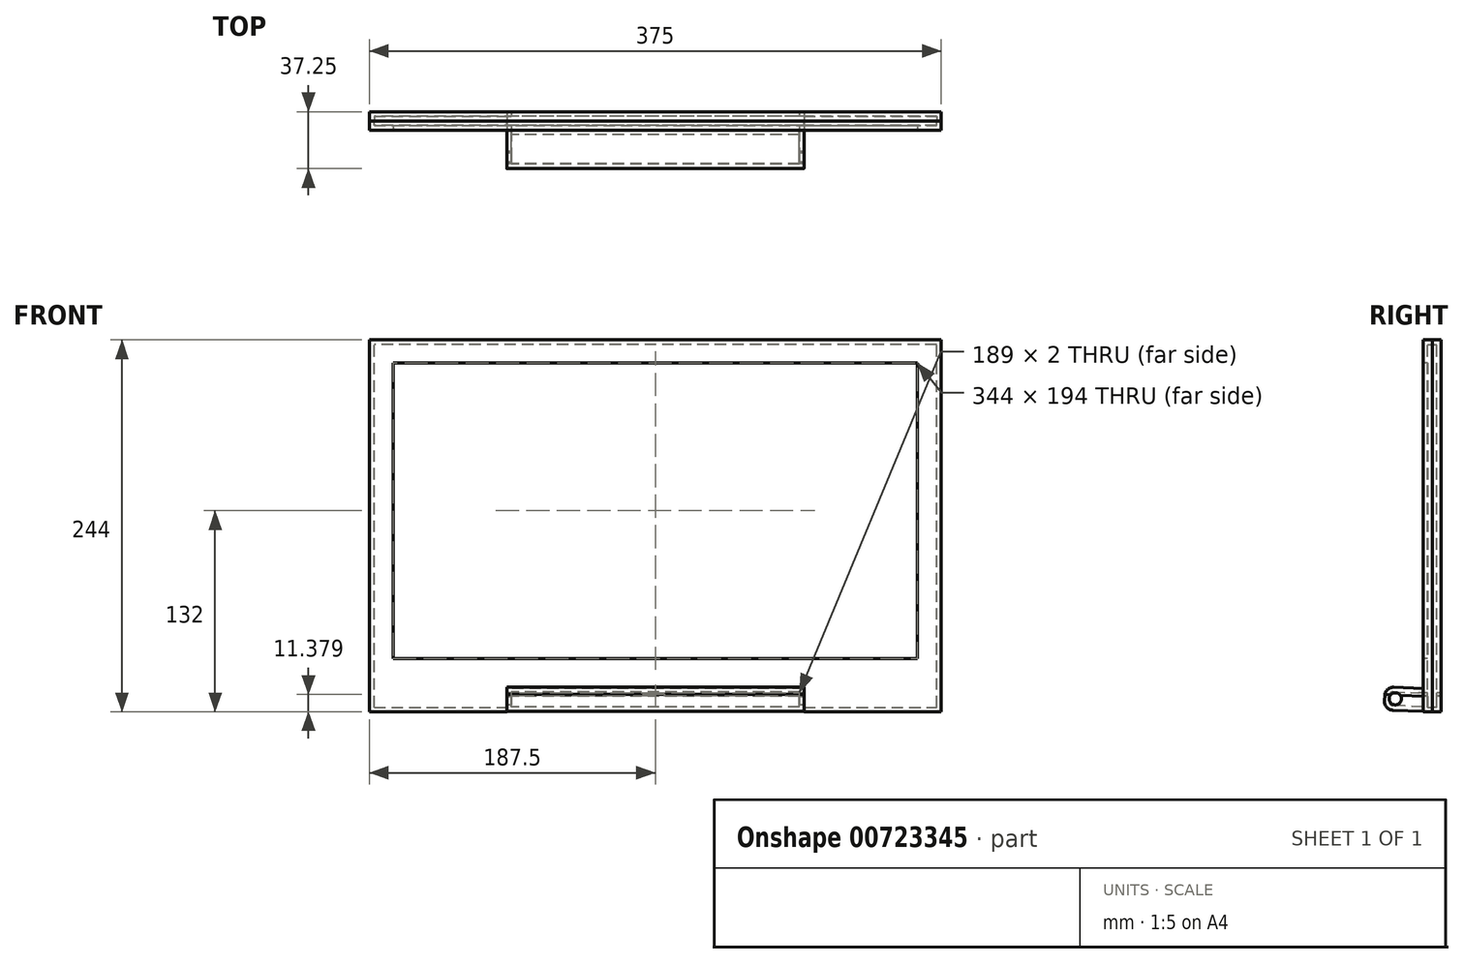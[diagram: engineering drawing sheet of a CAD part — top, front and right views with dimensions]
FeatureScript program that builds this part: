
annotation { "Feature Type Name" : "Feature", "Feature Type Description" : "" }
export const myFeature = defineFeature(function(context is Context, id is Id, definition is map)
    precondition{}
    {
        {
            var Q0;
            Q0=qCreatedBy(makeId("Front.planeOp"),FACE);
            var sketch = newSketch(context, id + "F0", { "sketchPlane" : qUnion([Q0])});
            skLineSegment(sketch, "E0.bottom", {"start": v(187.5, -117) * mm, "end": v(-187.5, -117) * mm});
            skLineSegment(sketch, "E0.top", {"start": v(187.5, 117) * mm, "end": v(-187.5, 117) * mm});
            skLineSegment(sketch, "E0.left", {"start": v(187.5, -117) * mm, "end": v(187.5, 117) * mm});
            skLineSegment(sketch, "E0.right", {"start": v(-187.5, -117) * mm, "end": v(-187.5, 117) * mm});
            skPoint(sketch, "E0.middle", {"position": v(0, 0) * mm});
            skSolve(sketch);
        }
        {
            var Q0;
            Q0=makeQuery(id+"F0.imprint","IMPRINT",FACE,{"disambiguationData":[TD([[makeQuery(id+"F0.imprint","IMPRINT",EDGE,{"derivedFrom":sQuery(id+"F0.wireOp",EDGE,"E0.bottom")}),-1.0]])]});
            extrude(context, id + "F1", {"entities" : qUnion([Q0]), "depth" : 6 * mm, "offsetDistance" : 25 * mm});
        }
        {
            var Q0;
            Q0=makeQuery(id+"F1.opExtrude","CAP_FACE",FACE,{"disambiguationData":[OSD([sQuery(id+"F0.wireOp",EDGE,"E0.bottom"),sQuery(id+"F0.wireOp",EDGE,"E0.top"),sQuery(id+"F0.wireOp",EDGE,"E0.left"),sQuery(id+"F0.wireOp",EDGE,"E0.right")])],"isStart":false});
            var sketch = newSketch(context, id + "F2", { "sketchPlane" : qUnion([Q0])});
            skLineSegment(sketch, "E1.bottom", {"start": v(-187.5, -117) * mm, "end": v(187.5, -117) * mm});
            skLineSegment(sketch, "E1.top", {"start": v(-187.5, -127) * mm, "end": v(187.5, -127) * mm});
            skLineSegment(sketch, "E1.left", {"start": v(-187.5, -117) * mm, "end": v(-187.5, -127) * mm});
            skLineSegment(sketch, "E1.right", {"start": v(187.5, -117) * mm, "end": v(187.5, -127) * mm});
            skSolve(sketch);
        }
        {
            var Q0;
            Q0=qSketchRegion(id+"F2",true);
            extrude(context, id + "F3", {"entities" : qUnion([Q0]), "operationType" : NewBodyOperationType.ADD, "oppositeDirection" : true, "depth" : 6 * mm, "offsetDistance" : 25 * mm});
        }
        {
            var Q0;
            Q0=makeQuery(id+"F3.boolean.opBoolean","MERGE",FACE,{"derivedFrom":[makeQuery(id+"F1.opExtrude","CAP_FACE",FACE,{"disambiguationData":[OSD([sQuery(id+"F0.wireOp",EDGE,"E0.bottom"),sQuery(id+"F0.wireOp",EDGE,"E0.top"),sQuery(id+"F0.wireOp",EDGE,"E0.left"),sQuery(id+"F0.wireOp",EDGE,"E0.right")])],"isStart":false}),makeQuery(id+"F3.opExtrude","CAP_FACE",FACE,{"disambiguationData":[OSD([sQuery(id+"F2.wireOp",EDGE,"E1.bottom"),sQuery(id+"F2.wireOp",EDGE,"E1.top"),sQuery(id+"F2.wireOp",EDGE,"E1.left"),sQuery(id+"F2.wireOp",EDGE,"E1.right")])],"isStart":true})]});
            shell(context, id + "F4", {"entities" : qUnion([Q0]), "thickness" : 3 * mm});
        }
        {
            var Q0;
            Q0=makeQuery(id+"F3.boolean.opBoolean","MERGE",FACE,{"derivedFrom":[makeQuery(id+"F1.opExtrude","CAP_FACE",FACE,{"disambiguationData":[OSD([sQuery(id+"F0.wireOp",EDGE,"E0.bottom"),sQuery(id+"F0.wireOp",EDGE,"E0.top"),sQuery(id+"F0.wireOp",EDGE,"E0.left"),sQuery(id+"F0.wireOp",EDGE,"E0.right")])],"isStart":false}),makeQuery(id+"F3.opExtrude","CAP_FACE",FACE,{"disambiguationData":[OSD([sQuery(id+"F2.wireOp",EDGE,"E1.bottom"),sQuery(id+"F2.wireOp",EDGE,"E1.top"),sQuery(id+"F2.wireOp",EDGE,"E1.left"),sQuery(id+"F2.wireOp",EDGE,"E1.right")])],"isStart":true})]});
            var sketch = newSketch(context, id + "F5", { "sketchPlane" : qUnion([Q0])});
            skLineSegment(sketch, "E2.bottom", {"start": v(-187.5, 117) * mm, "end": v(187.5, 117) * mm});
            skLineSegment(sketch, "E2.top", {"start": v(-187.5, -127) * mm, "end": v(187.5, -127) * mm});
            skLineSegment(sketch, "E2.left", {"start": v(-187.5, 117) * mm, "end": v(-187.5, -127) * mm});
            skLineSegment(sketch, "E2.right", {"start": v(187.5, 117) * mm, "end": v(187.5, -127) * mm});
            skSolve(sketch);
        }
        {
            var Q0;
            Q0=qSketchRegion(id+"F5",true);
            extrude(context, id + "F6", {"entities" : qUnion([Q0]), "depth" : 6 * mm, "offsetDistance" : 25 * mm});
        }
        {
            var Q0;
            Q0=makeQuery(id+"F6.opExtrude","CAP_FACE",FACE,{"disambiguationData":[OSD([sQuery(id+"F5.wireOp",EDGE,"E2.bottom"),sQuery(id+"F5.wireOp",EDGE,"E2.top"),sQuery(id+"F5.wireOp",EDGE,"E2.left"),sQuery(id+"F5.wireOp",EDGE,"E2.right")])],"isStart":true});
            shell(context, id + "F7", {"entities" : qUnion([Q0]), "thickness" : 3 * mm});
        }
        {
            var Q0;
            Q0=makeQuery(id+"F6.opExtrude","CAP_FACE",FACE,{"disambiguationData":[OSD([sQuery(id+"F5.wireOp",EDGE,"E2.bottom"),sQuery(id+"F5.wireOp",EDGE,"E2.top"),sQuery(id+"F5.wireOp",EDGE,"E2.left"),sQuery(id+"F5.wireOp",EDGE,"E2.right")])],"isStart":false});
            var sketch = newSketch(context, id + "F8", { "sketchPlane" : qUnion([Q0])});
            skPoint(sketch, "E3", {"position": v(0, 0) * mm});
            skPoint(sketch, "E4", {"position": v(0, 5) * mm});
            skLineSegment(sketch, "E5.bottom", {"start": v(-172, 102) * mm, "end": v(172, 102) * mm});
            skLineSegment(sketch, "E5.top", {"start": v(-172, -92) * mm, "end": v(172, -92) * mm});
            skLineSegment(sketch, "E5.left", {"start": v(-172, 102) * mm, "end": v(-172, -92) * mm});
            skLineSegment(sketch, "E5.right", {"start": v(172, 102) * mm, "end": v(172, -92) * mm});
            skSolve(sketch);
        }
        {
            var Q0;
            Q0=qSketchRegion(id+"F8",true);
            extrude(context, id + "F9", {"entities" : qUnion([Q0]), "operationType" : NewBodyOperationType.REMOVE, "oppositeDirection" : true, "depth" : 3 * mm, "offsetDistance" : 25 * mm});
        }
        {
            var Q0;
            Q0=makeQuery(id+"F6.opExtrude","SWEPT_FACE",FACE,{"disambiguationData":[OSD([sQuery(id+"F5.wireOp",EDGE,"E2.left")])]});
            var sketch = newSketch(context, id + "F10", { "sketchPlane" : qUnion([Q0])});
            skLineSegment(sketch, "E6", {"start": v(6, -127) * mm, "end": v(37.47, -125.7) * mm});
            skLineSegment(sketch, "E7", {"start": v(37.47, -125.7) * mm, "end": v(36.86, -110.72) * mm});
            skLineSegment(sketch, "E8", {"start": v(36.86, -110.72) * mm, "end": v(12, -111.74) * mm});
            skPoint(sketch, "E9", {"position": v(37.06, -115.72) * mm});
            skLineSegment(sketch, "E10", {"start": v(37.06, -115.72) * mm, "end": v(12, -116.75) * mm});
            skLineSegment(sketch, "E11", {"start": v(12, -111.74) * mm, "end": v(12, -116.75) * mm});
            skLineSegment(sketch, "E12", {"start": v(12, -116.75) * mm, "end": v(6, -117) * mm});
            skLineSegment(sketch, "E13", {"start": v(6, -117) * mm, "end": v(6, -127) * mm});
            skSolve(sketch);
        }
        {
            var Q0;
            {var subQ0=sQuery(id+"F10.wireOp",EDGE,"E8");Q0=makeQuery(id+"F10.imprint","IMPRINT",FACE,{"disambiguationData":[TD([[makeQuery(id+"F10.imprint","IMPRINT",EDGE,{"derivedFrom":subQ0}),1.0]])]});}
            extrude(context, id + "F11", {"entities" : qUnion([Q0]), "oppositeDirection" : true, "depth" : 195 * mm, "offsetDistance" : 25 * mm});
        }
        {
            var Q0;
            {var subQ5=sQuery(id+"F10.wireOp",EDGE,"E10");Q0=makeQuery(id+"F10.imprint","IMPRINT",FACE,{"disambiguationData":[TD([[makeQuery(id+"F10.imprint","IMPRINT",EDGE,{"derivedFrom":subQ5}),1.0]])]});}
            var Q1;
            {var subQ5=sQuery(id+"F10.wireOp",EDGE,"E12");Q1=makeQuery(id+"F10.imprint","IMPRINT",FACE,{"disambiguationData":[TD([[makeQuery(id+"F10.imprint","IMPRINT",EDGE,{"derivedFrom":subQ5}),1.0]])]});}
            extrude(context, id + "F12", {"entities" : qUnion([Q0, Q1]), "oppositeDirection" : true, "depth" : 195 * mm, "offsetDistance" : 25 * mm});
        }
        {
            var Q0;
            Q0=makeQuery(id+"F11.opExtrude","SWEPT_BODY",BODY,{"disambiguationData":[OSD([sQuery(id+"F10.wireOp",EDGE,"E7"),sQuery(id+"F10.wireOp",EDGE,"E8"),sQuery(id+"F10.wireOp",EDGE,"E10"),sQuery(id+"F10.wireOp",EDGE,"E11")])]});
            var Q1;
            Q1=makeQuery(id+"F12.opExtrude","SWEPT_BODY",BODY,{"disambiguationData":[OSD([sQuery(id+"F10.wireOp",EDGE,"E6"),sQuery(id+"F10.wireOp",EDGE,"E7"),sQuery(id+"F10.wireOp",EDGE,"E10"),sQuery(id+"F10.wireOp",EDGE,"E12"),sQuery(id+"F10.wireOp",EDGE,"E13")])]});
            transform(context, id + "F13", {"entities" : qUnion([Q0, Q1]), "transformType" : TransformType.TRANSLATION_3D, "dx" : 90 * mm, "dy" : 0 * mm, "dz" : 0 * mm, "makeCopy" : false});
        }
        {
            var Q0;
            Q0=makeQuery(id+"F11.opExtrude","SWEPT_EDGE",EDGE,{"disambiguationData":[OSD([sQuery(id+"F10.wireOp",EDGE,"E7"),sQuery(id+"F10.wireOp",EDGE,"E8")])]});
            var Q1;
            Q1=makeQuery(id+"F12.opExtrude","SWEPT_EDGE",EDGE,{"disambiguationData":[OSD([sQuery(id+"F10.wireOp",EDGE,"E6"),sQuery(id+"F10.wireOp",EDGE,"E7")])]});
            fillet(context, id + "F14", {"entities" : qUnion([Q0, Q1]), "radius" : 5.5 * mm, "tangentPropagation" : true, "allowEdgeOverflow" : false});
        }
        {
            var Q0;
            Q0=makeQuery(id+"F11.opExtrude","SWEPT_FACE",FACE,{"disambiguationData":[OSD([sQuery(id+"F10.wireOp",EDGE,"E10")])]});
            shell(context, id + "F15", {"entities" : qUnion([Q0]), "thickness" : 3 * mm});
        }
        {
            var Q0;
            Q0=makeQuery(id+"F12.opExtrude","SWEPT_FACE",FACE,{"disambiguationData":[OSD([sQuery(id+"F10.wireOp",EDGE,"E10"),sQuery(id+"F10.wireOp",EDGE,"E12")])]});
            shell(context, id + "F16", {"entities" : qUnion([Q0]), "thickness" : 3 * mm});
        }
        {
            var Q0;
            Q0=makeQuery(id+"F16.opShell","OFFSET_FACE",FACE,{"disambiguationData":[OSD([sQuery(id+"F10.wireOp",EDGE,"E13")])]});
            extrude(context, id + "F17", {"entities" : qUnion([Q0]), "operationType" : NewBodyOperationType.REMOVE, "oppositeDirection" : true, "depth" : 25 * mm, "offsetDistance" : 25 * mm});
        }
        {
            var Q0;
            Q0=makeQuery(id+"F15.opShell","OFFSET_FACE",FACE,{"disambiguationData":[OSD([sQuery(id+"F10.wireOp",EDGE,"E11")])]});
            extrude(context, id + "F18", {"entities" : qUnion([Q0]), "operationType" : NewBodyOperationType.REMOVE, "oppositeDirection" : true, "depth" : 25 * mm, "offsetDistance" : 25 * mm});
        }
        {
            var Q0;
            Q0=makeQuery(id+"F11.opExtrude","SWEPT_FACE",FACE,{"disambiguationData":[OSD([sQuery(id+"F10.wireOp",EDGE,"E10")])]});
            var sketch = newSketch(context, id + "F19", { "sketchPlane" : qUnion([Q0])});
            skPoint(sketch, "E14", {"position": v(94.5, 7.2) * mm});
            skLineSegment(sketch, "E15.bottom", {"start": v(-94.5, 10.2) * mm, "end": v(94.5, 10.2) * mm});
            skLineSegment(sketch, "E15.top", {"start": v(-94.5, 7.2) * mm, "end": v(94.5, 7.2) * mm});
            skLineSegment(sketch, "E15.left", {"start": v(-94.5, 10.2) * mm, "end": v(-94.5, 7.2) * mm});
            skLineSegment(sketch, "E15.right", {"start": v(94.5, 10.2) * mm, "end": v(94.5, 7.2) * mm});
            skSolve(sketch);
        }
        {
            var Q0;
            Q0=qSketchRegion(id+"F19",true);
            extrude(context, id + "F20", {"entities" : qUnion([Q0]), "operationType" : NewBodyOperationType.REMOVE, "oppositeDirection" : true, "depth" : 2 * mm, "offsetDistance" : 25 * mm});
        }
        {
            var Q0;
            Q0=makeQuery(id+"F6.opExtrude","CAP_FACE",FACE,{"disambiguationData":[OSD([sQuery(id+"F5.wireOp",EDGE,"E2.bottom"),sQuery(id+"F5.wireOp",EDGE,"E2.top"),sQuery(id+"F5.wireOp",EDGE,"E2.left"),sQuery(id+"F5.wireOp",EDGE,"E2.right")])],"isStart":false});
            var sketch = newSketch(context, id + "F21", { "sketchPlane" : qUnion([Q0])});
            skPoint(sketch, "E16", {"position": v(-97.5, -127) * mm});
            skPoint(sketch, "E17", {"position": v(97.5, -127) * mm});
            skLineSegment(sketch, "E18", {"start": v(-97.5, -127) * mm, "end": v(-97.5, -116.7) * mm});
            skLineSegment(sketch, "E19", {"start": v(-97.5, -116.7) * mm, "end": v(-94.5, -116.7) * mm});
            skLineSegment(sketch, "E20", {"start": v(-94.5, -116.7) * mm, "end": v(-94.5, -114.7) * mm});
            skLineSegment(sketch, "E21", {"start": v(97.5, -127) * mm, "end": v(97.5, -116.7) * mm});
            skLineSegment(sketch, "E22", {"start": v(97.5, -116.7) * mm, "end": v(94.5, -116.7) * mm});
            skLineSegment(sketch, "E23", {"start": v(94.5, -116.7) * mm, "end": v(94.5, -114.7) * mm});
            skLineSegment(sketch, "E24", {"start": v(-94.5, -114.7) * mm, "end": v(94.5, -114.7) * mm});
            skSolve(sketch);
        }
        {
            var Q0;
            {var subQ1=sQuery(id+"F21.wireOp",EDGE,"E18");Q0=makeQuery(id+"F21.imprint","IMPRINT",FACE,{"disambiguationData":[TD([[makeQuery(id+"F21.imprint","IMPRINT",EDGE,{"derivedFrom":subQ1}),-1.0]])]});}
            extrude(context, id + "F22", {"entities" : qUnion([Q0]), "operationType" : NewBodyOperationType.REMOVE, "oppositeDirection" : true, "depth" : 25 * mm, "offsetDistance" : 25 * mm});
        }
        {
            var Q0;
            Q0=makeQuery(id+"F12.opExtrude","CAP_FACE",FACE,{"disambiguationData":[OSD([sQuery(id+"F10.wireOp",EDGE,"E6"),sQuery(id+"F10.wireOp",EDGE,"E7"),sQuery(id+"F10.wireOp",EDGE,"E10"),sQuery(id+"F10.wireOp",EDGE,"E12"),sQuery(id+"F10.wireOp",EDGE,"E13")])],"isStart":true});
            var sketch = newSketch(context, id + "F23", { "sketchPlane" : qUnion([Q0])});
            skPoint(sketch, "E25", {"position": v(6, -124) * mm});
            skPoint(sketch, "E26", {"position": v(9, -116.87) * mm});
            skLineSegment(sketch, "E27", {"start": v(6, -117) * mm, "end": v(6, -124) * mm});
            skLineSegment(sketch, "E28", {"start": v(6, -117) * mm, "end": v(9, -116.87) * mm});
            skLineSegment(sketch, "E29", {"start": v(9, -123.88) * mm, "end": v(6, -124) * mm});
            skLineSegment(sketch, "E30", {"start": v(9, -116.87) * mm, "end": v(9, -123.88) * mm});
            skSolve(sketch);
        }
        {
            var Q0;
            Q0=qSketchRegion(id+"F23",true);
            extrude(context, id + "F24", {"entities" : qUnion([Q0]), "operationType" : NewBodyOperationType.REMOVE, "oppositeDirection" : true, "depth" : 240 * mm, "offsetDistance" : 25 * mm});
        }
        {
            var Q0;
            Q0=makeQuery(id+"F12.opExtrude","CAP_FACE",FACE,{"disambiguationData":[OSD([sQuery(id+"F10.wireOp",EDGE,"E6"),sQuery(id+"F10.wireOp",EDGE,"E7"),sQuery(id+"F10.wireOp",EDGE,"E10"),sQuery(id+"F10.wireOp",EDGE,"E12"),sQuery(id+"F10.wireOp",EDGE,"E13")])],"isStart":true});
            var sketch = newSketch(context, id + "F25", { "sketchPlane" : qUnion([Q0])});
            skPoint(sketch, "E31", {"position": v(37.17, -118.21) * mm});
            skPoint(sketch, "E32", {"position": v(30.17, -118.5) * mm});
            skCircle(sketch, "E33", {"center": v(30.17, -118.5) * mm, "radius": 4 * mm});
            skSolve(sketch);
        }
        {
            var Q0;
            Q0=sQuery(id+"F25.wireOp",VERTEX,"E32");
            var Q1;
            Q1=makeQuery(id+"F11.opExtrude","SWEPT_BODY",BODY,{"disambiguationData":[OSD([sQuery(id+"F10.wireOp",EDGE,"E7"),sQuery(id+"F10.wireOp",EDGE,"E8"),sQuery(id+"F10.wireOp",EDGE,"E10"),sQuery(id+"F10.wireOp",EDGE,"E11")])]});
            var Q2;
            Q2=makeQuery(id+"F12.opExtrude","SWEPT_BODY",BODY,{"disambiguationData":[OSD([sQuery(id+"F10.wireOp",EDGE,"E6"),sQuery(id+"F10.wireOp",EDGE,"E7"),sQuery(id+"F10.wireOp",EDGE,"E10"),sQuery(id+"F10.wireOp",EDGE,"E12"),sQuery(id+"F10.wireOp",EDGE,"E13")])]});
            hole(context, id + "F26", {"style" : HoleStyle.SIMPLE, "endStyle" : HoleEndStyle.THROUGH, "holeDiameter" : 8 * mm, "majorDiameter" : 5 * mm, "isTappedThrough" : true, "tappedDepth" : 12 * mm, "tapClearance" : 3, "locations" : qUnion([Q0]), "scope" : qUnion([Q1, Q2])});
        }
    });
